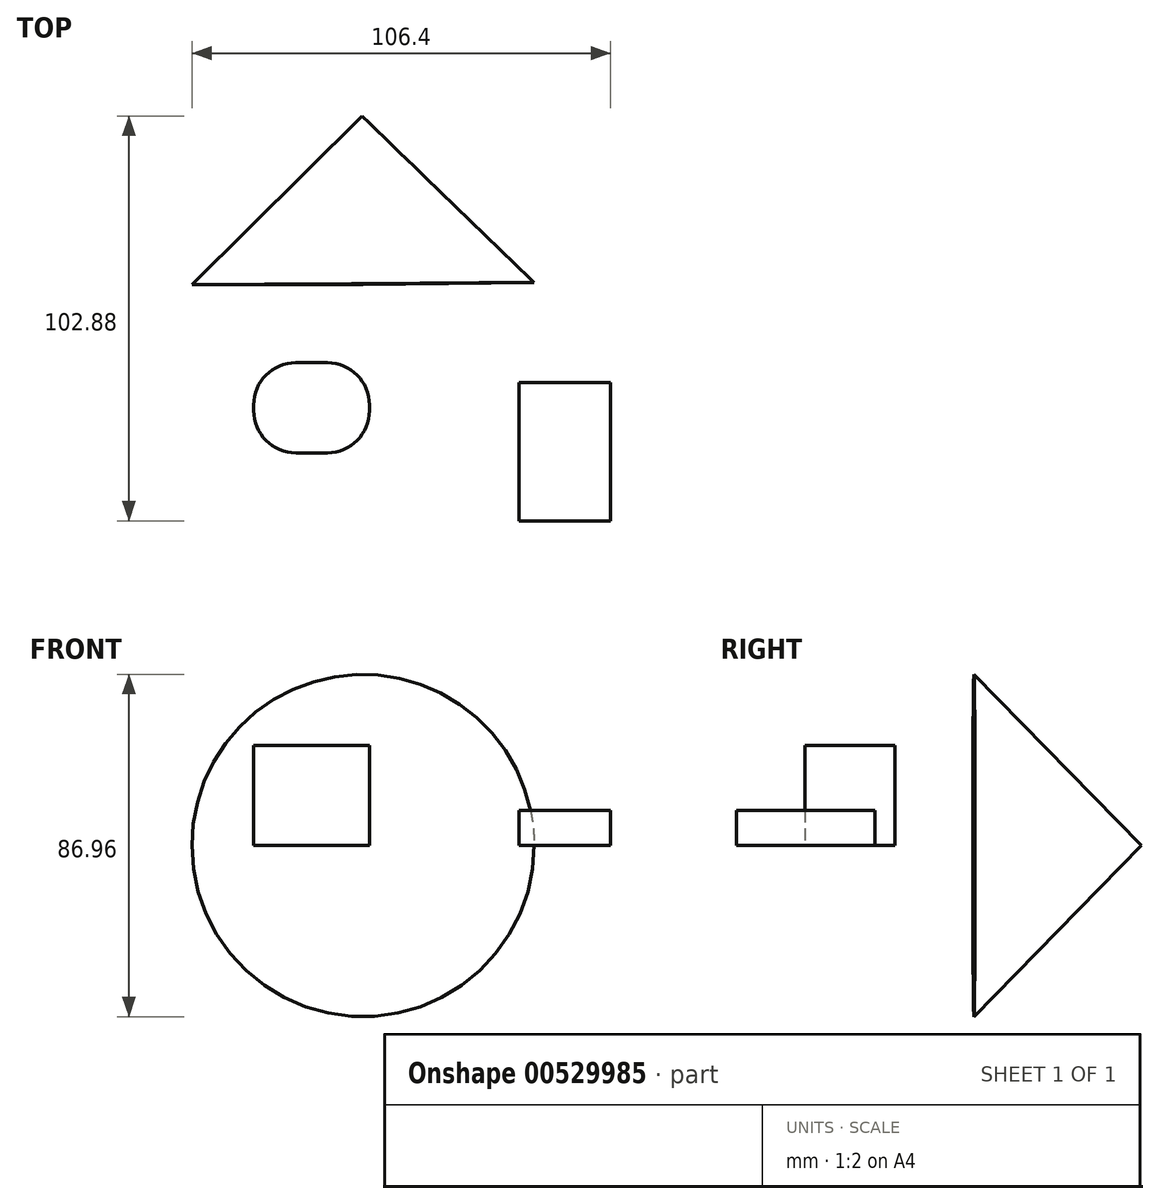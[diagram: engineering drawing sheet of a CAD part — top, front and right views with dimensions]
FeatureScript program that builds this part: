
annotation { "Feature Type Name" : "Feature", "Feature Type Description" : "" }
export const myFeature = defineFeature(function(context is Context, id is Id, definition is map)
    precondition{}
    {
        {
            var Q0;
            Q0=qCreatedBy(makeId("Top.planeOp"),FACE);
            var sketch = newSketch(context, id + "F0", { "sketchPlane" : qUnion([Q0])});
            skLineSegment(sketch, "E0", {"start": v(-27.21, 51.02) * mm, "end": v(-70.4, 8.13) * mm});
            skLineSegment(sketch, "E1", {"start": v(-70.4, 8.13) * mm, "end": v(-26.92, 8.13) * mm});
            skLineSegment(sketch, "E2", {"start": v(-27.21, 51.02) * mm, "end": v(-26.92, 8.13) * mm});
            skSolve(sketch);
        }
        {
            var Q0;
            Q0 = qSketchRegion(id + "F0", true);
            var Q1;
            Q1=sQuery(id+"F0.wireOp",EDGE,"E2");
            revolve(context, id + "F1", {"entities" : qUnion([Q0]), "axis" : qUnion([Q1]), "revolveType" : RevolveType.FULL});
        }
        {
            var Q0;
            Q0=qCreatedBy(makeId("Top.planeOp"),FACE);
            var sketch = newSketch(context, id + "F2", { "sketchPlane" : qUnion([Q0])});
            skLineSegment(sketch, "E3.bottom", {"start": v(-43.99, -11.67) * mm, "end": v(-35.99, -11.67) * mm});
            skLineSegment(sketch, "E3.top", {"start": v(-43.98, -34.56) * mm, "end": v(-35.99, -34.56) * mm});
            skLineSegment(sketch, "E3.left", {"start": v(-54.7, -22.38) * mm, "end": v(-54.7, -23.84) * mm});
            skLineSegment(sketch, "E3.right", {"start": v(-25.27, -22.4) * mm, "end": v(-25.27, -23.84) * mm});
            skPoint(sketch, "E4.visualSharp", {"position": v(-54.7, -11.67) * mm});
            skArc(sketch, "E4.filletArc", {"start": v(-43.99, -11.67) * mm, "mid": v(-51.56, -14.8) * mm, "end": v(-54.7, -22.38) * mm});
            skPoint(sketch, "E5.visualSharp", {"position": v(-25.27, -11.67) * mm});
            skArc(sketch, "E5.filletArc", {"start": v(-25.27, -22.4) * mm, "mid": v(-28.41, -14.81) * mm, "end": v(-35.99, -11.67) * mm});
            skPoint(sketch, "E6.visualSharp", {"position": v(-54.7, -34.56) * mm});
            skArc(sketch, "E6.filletArc", {"start": v(-54.7, -23.84) * mm, "mid": v(-51.55, -31.42) * mm, "end": v(-43.98, -34.56) * mm});
            skPoint(sketch, "E7.visualSharp", {"position": v(-25.27, -34.56) * mm});
            skArc(sketch, "E7.filletArc", {"start": v(-35.99, -34.56) * mm, "mid": v(-28.41, -31.42) * mm, "end": v(-25.27, -23.84) * mm});
            skSolve(sketch);
        }
        {
            var Q0;
            Q0 = qSketchRegion(id + "F2", true);
            extrude(context, id + "F3", {"entities" : qUnion([Q0]), "depth" : 25.4 * mm, "offsetDistance" : 25.4 * mm});
        }
        {
            var Q0;
            Q0=qCreatedBy(makeId("Top.planeOp"),FACE);
            var sketch = newSketch(context, id + "F4", { "sketchPlane" : qUnion([Q0])});
            skLineSegment(sketch, "E8.bottom", {"start": v(12.72, -16.66) * mm, "end": v(36, -16.66) * mm});
            skLineSegment(sketch, "E8.top", {"start": v(12.72, -51.86) * mm, "end": v(36, -51.86) * mm});
            skLineSegment(sketch, "E8.left", {"start": v(12.72, -16.66) * mm, "end": v(12.72, -51.86) * mm});
            skLineSegment(sketch, "E8.right", {"start": v(36, -16.66) * mm, "end": v(36, -51.86) * mm});
            skSolve(sketch);
        }
        {
            var Q0;
            Q0 = qSketchRegion(id + "F4", true);
            extrude(context, id + "F5", {"entities" : qUnion([Q0]), "depth" : 8.9 * mm, "offsetDistance" : 25.4 * mm});
        }
    });
